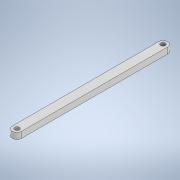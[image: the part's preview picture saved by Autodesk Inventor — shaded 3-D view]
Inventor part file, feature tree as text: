
AUTODESK INVENTOR PART (.ipt)
format: ipt  version: 2020 (Build 240168000, 168)  size: 102,912 bytes
history: native  units: mm
features: extrude x1, sketch x1
ambient origin geometry x8: Origin, YZ Plane, XZ Plane, XY Plane, X Axis, Y Axis, Z Axis, Center Point
bodies: Solid1 (feature_tree)
feature tree (2):
  extrude  "Extrusion1"  Depth=1.5mm
  sketch  "Sketch1"  dims[d0=3.0mm d1=1.5mm d2=47.7mm d3=2.0mm d4=0.0mm]
